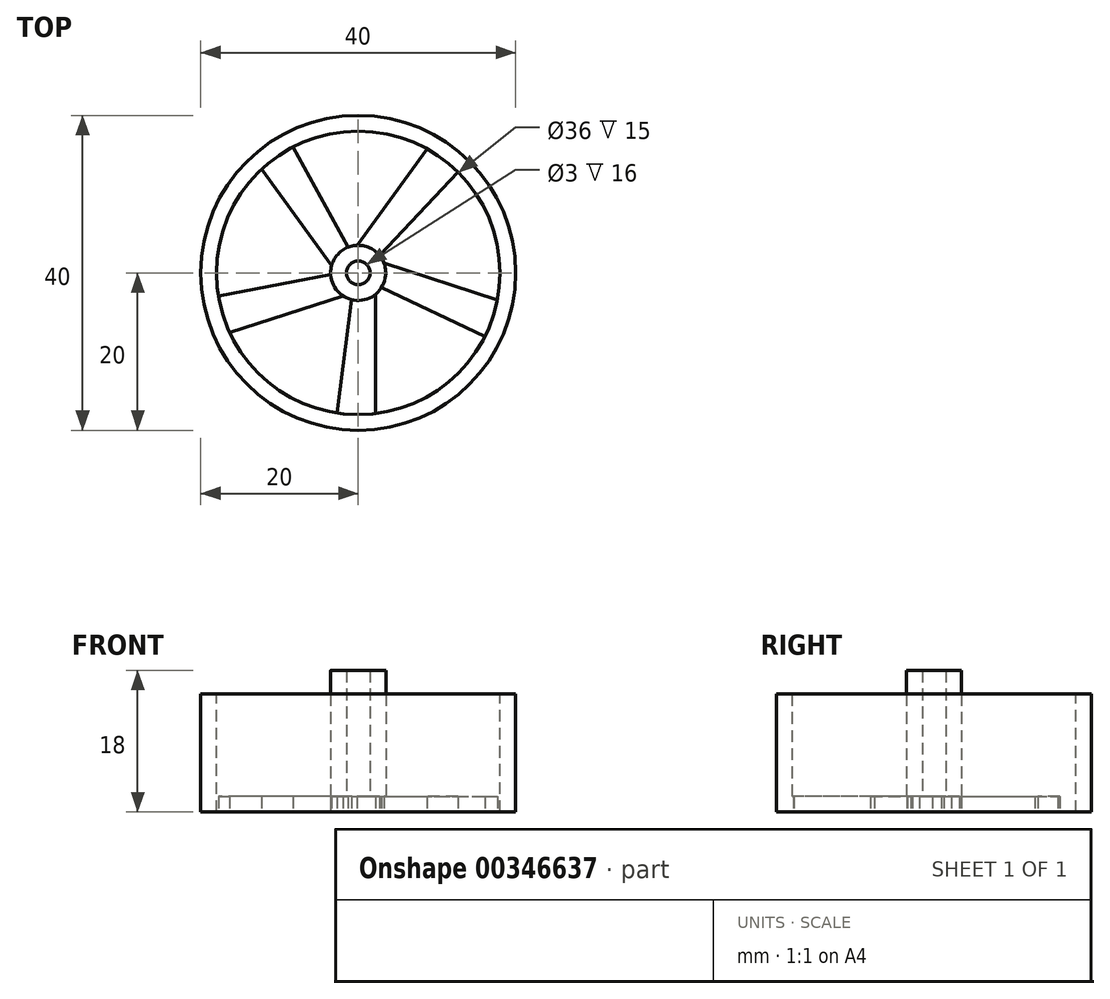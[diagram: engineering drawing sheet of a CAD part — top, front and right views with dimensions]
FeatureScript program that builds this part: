
annotation { "Feature Type Name" : "Feature", "Feature Type Description" : "" }
export const myFeature = defineFeature(function(context is Context, id is Id, definition is map)
    precondition{}
    {
        {
            var Q0;
            Q0=qCreatedBy(makeId("Top.planeOp"),FACE);
            var sketch = newSketch(context, id + "F0", { "sketchPlane" : qUnion([Q0])});
            skCircle(sketch, "E0", {"center": v(0, 0) * mm, "radius": 20 * mm});
            skSolve(sketch);
        }
        {
            var Q0;
            Q0=makeQuery(id+"F0.imprint","IMPRINT",FACE,{"disambiguationData":[TD([[makeQuery(id+"F0.imprint","IMPRINT",EDGE,{"derivedFrom":sQuery(id+"F0.wireOp",EDGE,"E0")}),1.0]])]});
            extrude(context, id + "F1", {"entities" : qUnion([Q0]), "depth" : 15 * mm});
        }
        {
            var Q0;
            Q0=makeQuery(id+"F1.opExtrude","CAP_FACE",FACE,{"disambiguationData":[OSD([sQuery(id+"F0.wireOp",EDGE,"E0")])],"isStart":false});
            var sketch = newSketch(context, id + "F2", { "sketchPlane" : qUnion([Q0])});
            skCircle(sketch, "E1", {"center": v(0, 0) * mm, "radius": 18 * mm});
            skSolve(sketch);
        }
        {
            var Q0;
            Q0=makeQuery(id+"F2.imprint","IMPRINT",FACE,{"disambiguationData":[TD([[makeQuery(id+"F2.imprint","IMPRINT",EDGE,{"derivedFrom":sQuery(id+"F2.wireOp",EDGE,"E1")}),1.0]])]});
            extrude(context, id + "F3", {"entities" : qUnion([Q0]), "operationType" : NewBodyOperationType.REMOVE, "oppositeDirection" : true, "depth" : 13 * mm});
        }
        {
            var Q0;
            Q0=makeQuery(id+"F3.boolean.opBoolean","COPY",FACE,{"derivedFrom":makeQuery(id+"F3.opExtrude","CAP_FACE",FACE,{"disambiguationData":[OSD([sQuery(id+"F2.wireOp",EDGE,"E1")])],"isStart":false})});
            var sketch = newSketch(context, id + "F4", { "sketchPlane" : qUnion([Q0])});
            skCircle(sketch, "E2", {"center": v(0, 0) * mm, "radius": 1.5 * mm});
            skCircle(sketch, "E3", {"center": v(0, 0) * mm, "radius": 3.5 * mm});
            skSolve(sketch);
        }
        {
            var Q0;
            Q0=makeQuery(id+"F4.imprint","IMPRINT",FACE,{"disambiguationData":[TD([[makeQuery(id+"F4.imprint","IMPRINT",EDGE,{"derivedFrom":sQuery(id+"F4.wireOp",EDGE,"E2")}),-1.0]])]});
            extrude(context, id + "F5", {"entities" : qUnion([Q0]), "operationType" : NewBodyOperationType.ADD, "depth" : 16 * mm});
        }
        {
            var Q0;
            Q0=makeQuery(id+"F1.opExtrude","CAP_FACE",FACE,{"disambiguationData":[OSD([sQuery(id+"F0.wireOp",EDGE,"E0")])],"isStart":true});
            var sketch = newSketch(context, id + "F6", { "sketchPlane" : qUnion([Q0])});
            skLineSegment(sketch, "E4", {"start": v(-0.87, 3.39) * mm, "end": v(-2.7, 17.8) * mm});
            skLineSegment(sketch, "E5", {"start": v(2.18, 2.74) * mm, "end": v(2.18, 17.87) * mm});
            skCircle(sketch, "E6", {"center": v(0, 0) * mm, "radius": 3.5 * mm});
            skCircle(sketch, "E7", {"center": v(0, 0) * mm, "radius": 18 * mm});
            skLineSegment(sketch, "E8.1.0", {"start": v(-1.93, 2.92) * mm, "end": v(-16.32, 7.6) * mm});
            skLineSegment(sketch, "E8.1.1", {"start": v(-3.5, 0.22) * mm, "end": v(-17.76, 2.93) * mm});
            skLineSegment(sketch, "E8.2.0", {"start": v(-3.37, -0.93) * mm, "end": v(-12.27, -13.17) * mm});
            skLineSegment(sketch, "E8.2.1", {"start": v(-1.29, -3.26) * mm, "end": v(-8.27, -15.99) * mm});
            skLineSegment(sketch, "E8.3.0", {"start": v(-0.15, -3.5) * mm, "end": v(8.74, -15.74) * mm});
            skLineSegment(sketch, "E8.3.1", {"start": v(2.7, -2.23) * mm, "end": v(12.65, -12.8) * mm});
            skLineSegment(sketch, "E8.4.0", {"start": v(3.28, -1.23) * mm, "end": v(17.67, 3.45) * mm});
            skLineSegment(sketch, "E8.4.1", {"start": v(2.95, 1.88) * mm, "end": v(16.09, 8.07) * mm});
            skSolve(sketch);
        }
        {
            var Q0;
            {var subQ0=sQuery(id+"F6.wireOp",EDGE,"E4");Q0=makeQuery(id+"F6.imprint","IMPRINT",FACE,{"disambiguationData":[TD([[makeQuery(id+"F6.imprint","IMPRINT",EDGE,{"derivedFrom":subQ0}),1.0]])]});}
            var Q1;
            {var subQ0=sQuery(id+"F6.wireOp",EDGE,"E8.1.1");Q1=makeQuery(id+"F6.imprint","IMPRINT",FACE,{"disambiguationData":[TD([[makeQuery(id+"F6.imprint","IMPRINT",EDGE,{"derivedFrom":subQ0}),1.0]])]});}
            var Q2;
            {var subQ0=sQuery(id+"F6.wireOp",EDGE,"E8.2.1");Q2=makeQuery(id+"F6.imprint","IMPRINT",FACE,{"disambiguationData":[TD([[makeQuery(id+"F6.imprint","IMPRINT",EDGE,{"derivedFrom":subQ0}),1.0]])]});}
            var Q3;
            {var subQ0=sQuery(id+"F6.wireOp",EDGE,"E8.3.1");Q3=makeQuery(id+"F6.imprint","IMPRINT",FACE,{"disambiguationData":[TD([[makeQuery(id+"F6.imprint","IMPRINT",EDGE,{"derivedFrom":subQ0}),1.0]])]});}
            var Q4;
            {var subQ0=sQuery(id+"F6.wireOp",EDGE,"E5");Q4=makeQuery(id+"F6.imprint","IMPRINT",FACE,{"disambiguationData":[TD([[makeQuery(id+"F6.imprint","IMPRINT",EDGE,{"derivedFrom":subQ0}),-1.0]])]});}
            extrude(context, id + "F7", {"entities" : qUnion([Q0, Q1, Q2, Q3, Q4]), "operationType" : NewBodyOperationType.REMOVE, "oppositeDirection" : true, "depth" : 2 * mm});
        }
    });
